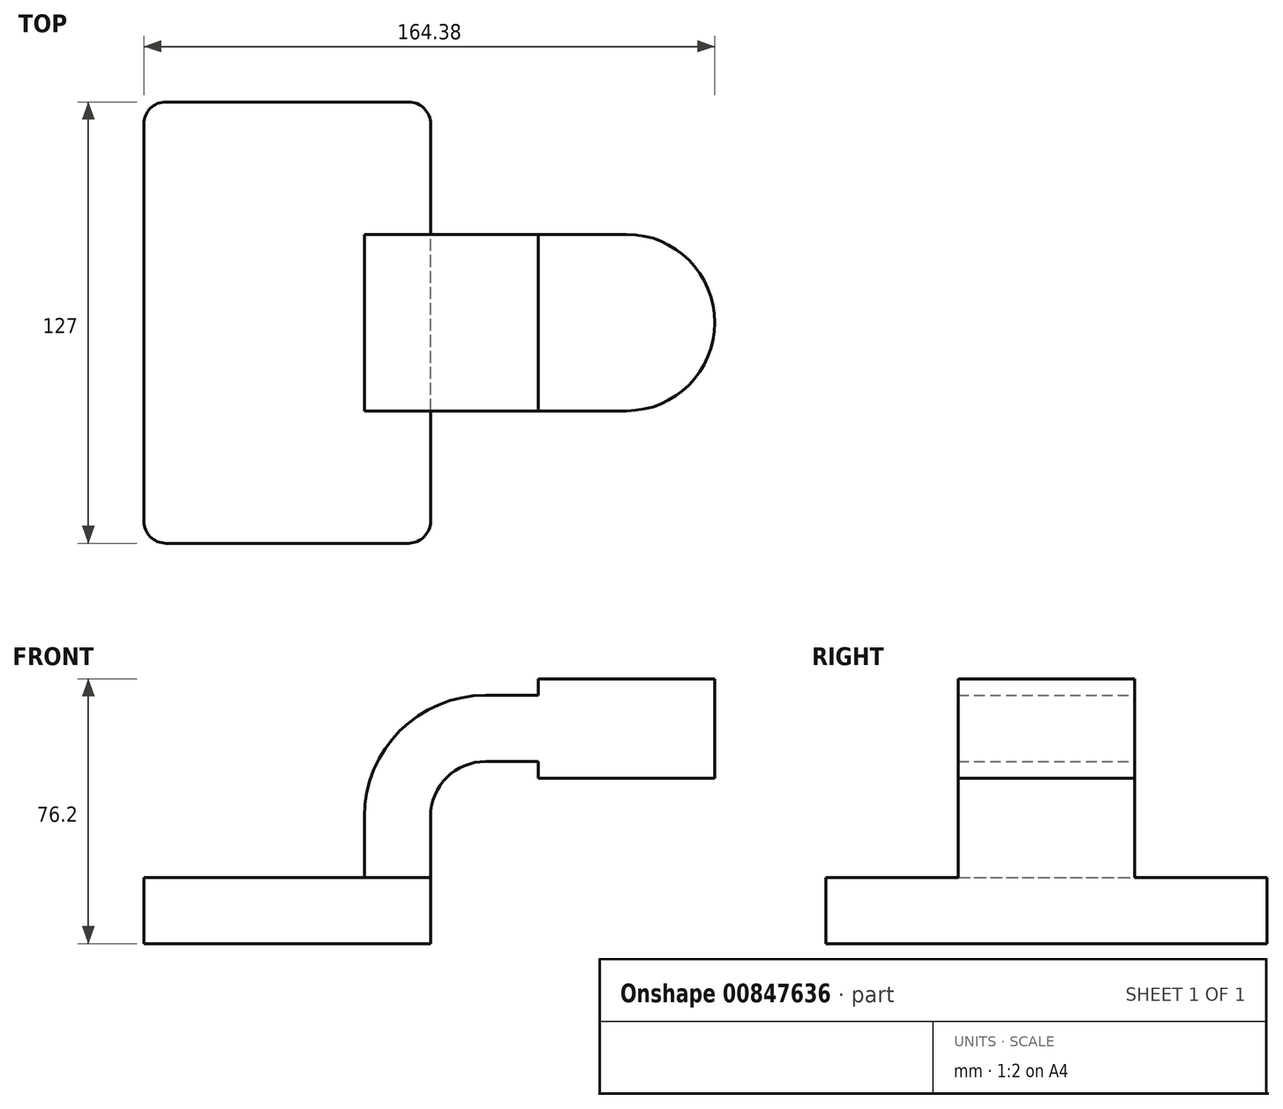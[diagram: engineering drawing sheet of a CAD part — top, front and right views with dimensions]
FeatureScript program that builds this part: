
annotation { "Feature Type Name" : "Feature", "Feature Type Description" : "" }
export const myFeature = defineFeature(function(context is Context, id is Id, definition is map)
    precondition{}
    {
        {
            var Q0;
            Q0=qCreatedBy(makeId("Front.planeOp"),FACE);
            var sketch = newSketch(context, id + "F0", { "sketchPlane" : qUnion([Q0])});
            skLineSegment(sketch, "E0.bottom", {"start": v(41.27, 9.53) * mm, "end": v(-41.28, 9.52) * mm});
            skLineSegment(sketch, "E0.top", {"start": v(41.28, -9.53) * mm, "end": v(-41.27, -9.53) * mm});
            skLineSegment(sketch, "E0.left", {"start": v(41.27, 9.53) * mm, "end": v(41.28, -9.53) * mm});
            skLineSegment(sketch, "E0.right", {"start": v(-41.28, 9.52) * mm, "end": v(-41.27, -9.53) * mm});
            skPoint(sketch, "E0.middle", {"position": v(0, 0) * mm});
            skLineSegment(sketch, "E1", {"start": v(41.27, 9.53) * mm, "end": v(41.27, 27) * mm});
            skArc(sketch, "E2", {"start": v(41.27, 27) * mm, "mid": v(45.92, 38.23) * mm, "end": v(57.15, 42.88) * mm});
            skLineSegment(sketch, "E3", {"start": v(57.15, 42.88) * mm, "end": v(97.7, 42.88) * mm});
            skLineSegment(sketch, "E4.bottom", {"start": v(123.1, 66.68) * mm, "end": v(72.3, 66.68) * mm});
            skLineSegment(sketch, "E4.top", {"start": v(123.1, 38.1) * mm, "end": v(72.3, 38.1) * mm});
            skLineSegment(sketch, "E4.left", {"start": v(123.1, 66.68) * mm, "end": v(123.1, 38.1) * mm});
            skLineSegment(sketch, "E4.right", {"start": v(72.3, 66.68) * mm, "end": v(72.3, 38.1) * mm});
            skPoint(sketch, "E4.middle", {"position": v(97.7, 52.39) * mm});
            skLineSegment(sketch, "E5.0", {"start": v(57.15, 61.93) * mm, "end": v(97.7, 61.93) * mm});
            skArc(sketch, "E5.1", {"start": v(22.22, 27) * mm, "mid": v(32.45, 51.7) * mm, "end": v(57.15, 61.93) * mm});
            skLineSegment(sketch, "E5.2", {"start": v(22.22, 9.53) * mm, "end": v(22.22, 27) * mm});
            skLineSegment(sketch, "E6", {"start": v(97.7, 38.1) * mm, "end": v(97.7, 66.68) * mm});
            skFitSpline(sketch, "E7", {"points": [v(-41.28, 9.52) * mm, v(57.15, 61.93) * mm], "startDerivative": vector(34.66, 136.88) * mm, "endDerivative": vector(97.73, -1.13) * mm});
            skSolve(sketch);
        }
        {
            var Q0;
            Q0=makeQuery(id+"F0.imprint","IMPRINT",FACE,{"disambiguationData":[TD([[makeQuery(id+"F0.imprint","IMPRINT",EDGE,{"derivedFrom":sQuery(id+"F0.wireOp",EDGE,"E0.top")}),-1.0]])]});
            extrude(context, id + "F1", {"entities" : qUnion([Q0]), "endBound" : BoundingType.SYMMETRIC, "depth" : 127 * mm, "offsetDistance" : 25.4 * mm, "hasSecondDirection" : true, "secondDirectionOppositeDirection" : true, "secondDirectionDepth" : 63.5 * mm});
        }
        {
            var Q0;
            {var subQ7=sQuery(id+"F0.wireOp",EDGE,"E1");Q0=makeQuery(id+"F0.imprint","IMPRINT",FACE,{"disambiguationData":[TD([[makeQuery(id+"F0.imprint","IMPRINT",EDGE,{"derivedFrom":subQ7}),1.0]])]});}
            var Q1;
            {var subQ0=sQuery(id+"F0.wireOp",EDGE,"E6");var subQ1=sQuery(id+"F0.wireOp",EDGE,"E3");var subQ2=makeQuery(id+"F0.imprint","INTERSECT",VERTEX,{"derivedFrom":[subQ1,subQ0]});Q1=makeQuery(id+"F0.imprint","IMPRINT",FACE,{"disambiguationData":[TD([[makeQuery(id+"F0.imprint","IMPRINT",EDGE,{"disambiguationData":[TD([[subQ2,1.0]])],"derivedFrom":subQ1}),1.0]])]});}
            var Q2;
            {var subQ0=sQuery(id+"F0.wireOp",EDGE,"E4.right");var subQ1=sQuery(id+"F0.wireOp",EDGE,"E4.bottom");var subQ2=makeQuery(id+"F0.imprint","INTERSECT",VERTEX,{"derivedFrom":[subQ1,subQ0]});Q2=makeQuery(id+"F0.imprint","IMPRINT",FACE,{"disambiguationData":[TD([[makeQuery(id+"F0.imprint","IMPRINT",EDGE,{"disambiguationData":[TD([[subQ2,1.0]])],"derivedFrom":subQ1}),1.0]])]});}
            var Q3;
            {var subQ0=sQuery(id+"F0.wireOp",EDGE,"E6");var subQ1=sQuery(id+"F0.wireOp",EDGE,"E3");var subQ2=makeQuery(id+"F0.imprint","INTERSECT",VERTEX,{"derivedFrom":[subQ1,subQ0]});Q3=makeQuery(id+"F0.imprint","IMPRINT",FACE,{"disambiguationData":[TD([[makeQuery(id+"F0.imprint","IMPRINT",EDGE,{"disambiguationData":[TD([[subQ2,1.0]])],"derivedFrom":subQ1}),-1.0]])]});}
            extrude(context, id + "F2", {"entities" : qUnion([Q0, Q1, Q2, Q3]), "operationType" : NewBodyOperationType.ADD, "endBound" : BoundingType.SYMMETRIC, "depth" : 50.8 * mm, "offsetDistance" : 25.4 * mm});
        }
        {
            var Q0;
            Q0=makeQuery(id+"F0.imprint","IMPRINT",FACE,{"disambiguationData":[TD([[makeQuery(id+"F0.imprint","IMPRINT",EDGE,{"derivedFrom":sQuery(id+"F0.wireOp",EDGE,"E5.1")}),1.0]])]});
            extrude(context, id + "F3", {"entities" : qUnion([Q0]), "operationType" : NewBodyOperationType.ADD, "endBound" : BoundingType.SYMMETRIC, "depth" : 15.88 * mm, "offsetDistance" : 25.4 * mm});
        }
        {
            var Q0;
            {var subQ0=sQuery(id+"F0.wireOp",EDGE,"E4.left");Q0=makeQuery(id+"F0.imprint","IMPRINT",FACE,{"disambiguationData":[TD([[makeQuery(id+"F0.imprint","IMPRINT",EDGE,{"derivedFrom":subQ0}),-1.0]])]});}
            var Q1;
            Q1=sQuery(id+"F0.wireOp",EDGE,"E6");
            revolve(context, id + "F4", {"operationType" : NewBodyOperationType.ADD, "surfaceOperationType" : NewSurfaceOperationType.NEW, "entities" : qUnion([Q0]), "axis" : qUnion([Q1]), "revolveType" : RevolveType.FULL});
        }
        {
            var Q0;
            Q0=makeQuery(id+"F1.opExtrude","CAP_EDGE",EDGE,{"disambiguationData":[OSD([sQuery(id+"F0.wireOp",EDGE,"E0.left")])],"isStart":false});
            var Q1;
            Q1=makeQuery(id+"F1.opExtrude","CAP_EDGE",EDGE,{"disambiguationData":[OSD([sQuery(id+"F0.wireOp",EDGE,"E0.left")])],"isStart":true});
            var Q2;
            Q2=makeQuery(id+"F1.opExtrude","CAP_EDGE",EDGE,{"disambiguationData":[OSD([sQuery(id+"F0.wireOp",EDGE,"E0.right")])],"isStart":true});
            var Q3;
            Q3=makeQuery(id+"F1.opExtrude","CAP_EDGE",EDGE,{"disambiguationData":[OSD([sQuery(id+"F0.wireOp",EDGE,"E0.right")])],"isStart":false});
            fillet(context, id + "F5", {"entities" : qUnion([Q0, Q1, Q2, Q3]), "radius" : 6.35 * mm, "tangentPropagation" : true, "allowEdgeOverflow" : false});
        }
    });
